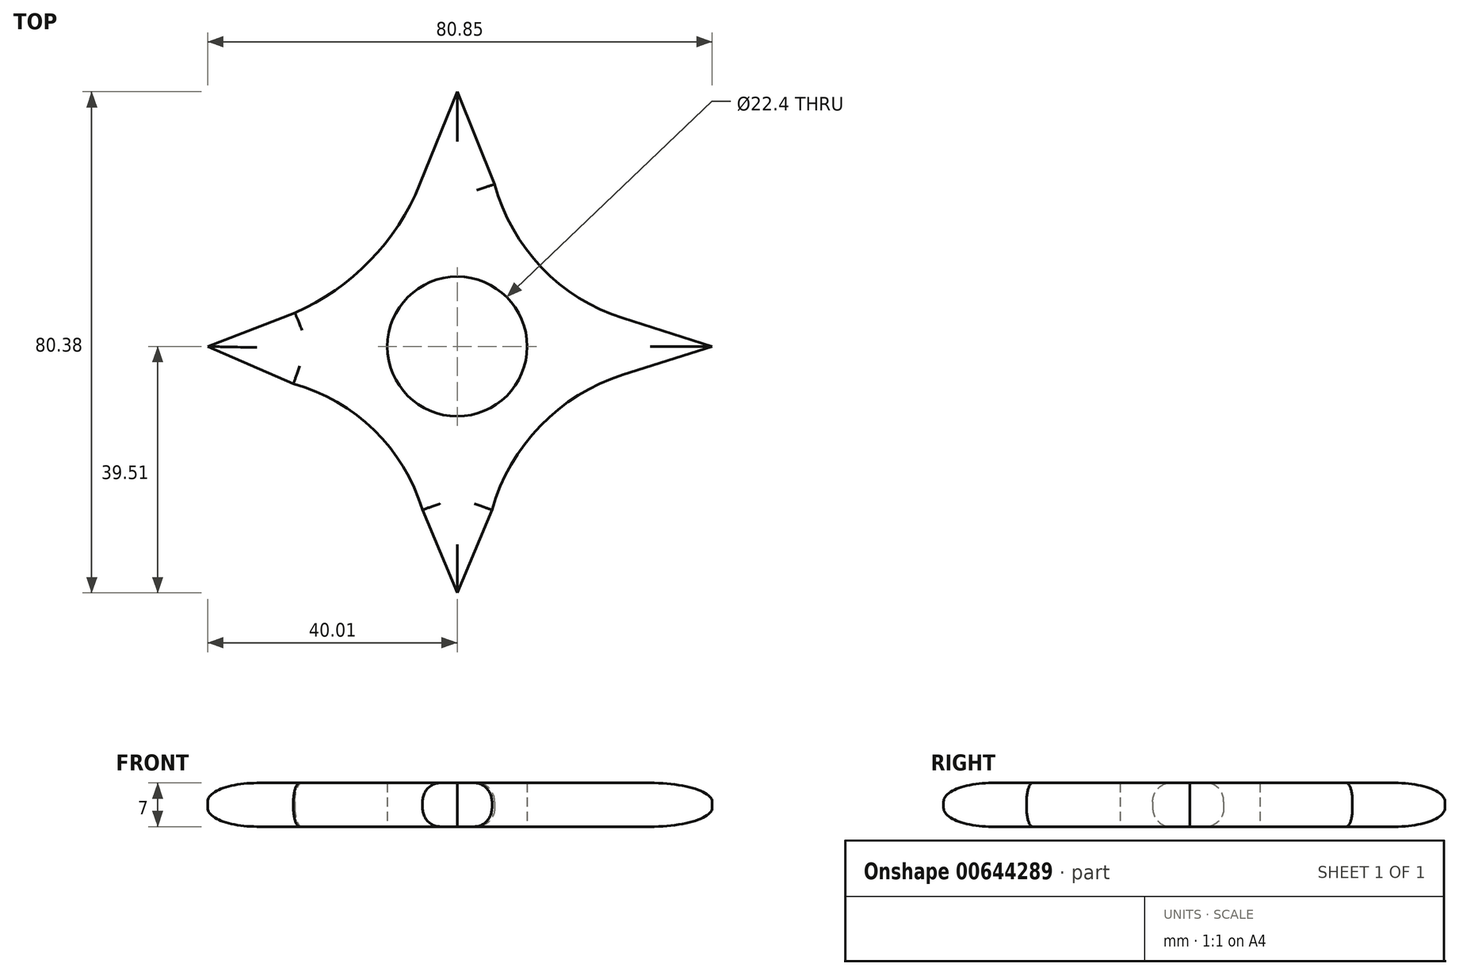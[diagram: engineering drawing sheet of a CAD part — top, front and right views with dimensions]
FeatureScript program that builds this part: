
annotation { "Feature Type Name" : "Feature", "Feature Type Description" : "" }
export const myFeature = defineFeature(function(context is Context, id is Id, definition is map)
    precondition{}
    {
        {
            var Q0;
            Q0=qCreatedBy(makeId("Top.planeOp"),FACE);
            var sketch = newSketch(context, id + "F0", { "sketchPlane" : qUnion([Q0])});
            skCircle(sketch, "E0", {"center": v(0, 0) * mm, "radius": 11.2 * mm});
            skLineSegment(sketch, "E1", {"start": v(0, 11.2) * mm, "end": v(0, 26.2) * mm});
            skLineSegment(sketch, "E2", {"start": v(11.2, 0) * mm, "end": v(26.2, 0) * mm});
            skLineSegment(sketch, "E3", {"start": v(0, -11.2) * mm, "end": v(0, -26.2) * mm});
            skLineSegment(sketch, "E4", {"start": v(-11.18, -0.6) * mm, "end": v(-26.17, 0) * mm});
            skLineSegment(sketch, "E5", {"start": v(0, -11.2) * mm, "end": v(5.57, -26.2) * mm});
            skLineSegment(sketch, "E6", {"start": v(0, -11.2) * mm, "end": v(-5.57, -26.2) * mm});
            skLineSegment(sketch, "E7", {"start": v(11.2, 0) * mm, "end": v(26.54, -4.54) * mm});
            skLineSegment(sketch, "E8", {"start": v(11.2, 0) * mm, "end": v(26.54, 4.54) * mm});
            skLineSegment(sketch, "E9", {"start": v(0, 11.2) * mm, "end": v(6, 26.03) * mm});
            skLineSegment(sketch, "E10", {"start": v(0, 11.2) * mm, "end": v(-6, 26.03) * mm});
            skLineSegment(sketch, "E11", {"start": v(-11.18, -0.6) * mm, "end": v(-26.02, 5.4) * mm});
            skLineSegment(sketch, "E12", {"start": v(-11.18, -0.6) * mm, "end": v(-26.25, -5.97) * mm});
            skLineSegment(sketch, "E13", {"start": v(-26.02, 5.4) * mm, "end": v(-40.01, 0) * mm});
            skLineSegment(sketch, "E14", {"start": v(-40.01, 0) * mm, "end": v(-26.25, -5.97) * mm});
            skLineSegment(sketch, "E15", {"start": v(-6, 26.03) * mm, "end": v(0, 40.87) * mm});
            skLineSegment(sketch, "E16", {"start": v(6, 26.03) * mm, "end": v(0, 40.87) * mm});
            skLineSegment(sketch, "E17", {"start": v(26.54, -4.54) * mm, "end": v(40.84, 0) * mm});
            skLineSegment(sketch, "E18", {"start": v(26.54, 4.54) * mm, "end": v(40.84, 0) * mm});
            skLineSegment(sketch, "E19", {"start": v(-5.57, -26.2) * mm, "end": v(0, -39.51) * mm});
            skLineSegment(sketch, "E20", {"start": v(0, -39.51) * mm, "end": v(5.57, -26.2) * mm});
            skPoint(sketch, "E21.visualSharp", {"position": v(6, 26.03) * mm});
            skLineSegment(sketch, "E21.filletArc", {"start": v(6, 26.03) * mm, "end": v(6, 26.03) * mm});
            skArc(sketch, "E22", {"start": v(6, 26.03) * mm, "mid": v(13.52, 12.66) * mm, "end": v(26.54, 4.54) * mm});
            skArc(sketch, "E23", {"start": v(-26.02, 5.4) * mm, "mid": v(-13.99, 13.76) * mm, "end": v(-6, 26.03) * mm});
            skArc(sketch, "E24", {"start": v(26.54, -4.54) * mm, "mid": v(13.32, -12.72) * mm, "end": v(5.57, -26.2) * mm});
            skArc(sketch, "E25", {"start": v(-5.57, -26.2) * mm, "mid": v(-13.31, -13.43) * mm, "end": v(-26.25, -5.97) * mm});
            skSolve(sketch);
        }
        {
            var Q0;
            Q0 = qSketchRegion(id + "F0", true);
            extrude(context, id + "F1", {"entities" : qUnion([Q0]), "depth" : 7 * mm, "offsetDistance" : 25 * mm});
        }
        {
            var Q0;
            Q0=makeQuery(id+"F1.opExtrude","CAP_EDGE",EDGE,{"disambiguationData":[OSD([sQuery(id+"F0.wireOp",EDGE,"E23")])],"isStart":true});
            var Q1;
            Q1=makeQuery(id+"F1.opExtrude","CAP_EDGE",EDGE,{"disambiguationData":[OSD([sQuery(id+"F0.wireOp",EDGE,"E13")])],"isStart":true});
            var Q2;
            Q2=makeQuery(id+"F1.opExtrude","CAP_EDGE",EDGE,{"disambiguationData":[OSD([sQuery(id+"F0.wireOp",EDGE,"E14")])],"isStart":true});
            var Q3;
            Q3=makeQuery(id+"F1.opExtrude","CAP_EDGE",EDGE,{"disambiguationData":[OSD([sQuery(id+"F0.wireOp",EDGE,"E25")])],"isStart":true});
            var Q4;
            Q4=makeQuery(id+"F1.opExtrude","CAP_EDGE",EDGE,{"disambiguationData":[OSD([sQuery(id+"F0.wireOp",EDGE,"E20")])],"isStart":true});
            var Q5;
            Q5=makeQuery(id+"F1.opExtrude","CAP_EDGE",EDGE,{"disambiguationData":[OSD([sQuery(id+"F0.wireOp",EDGE,"E19")])],"isStart":true});
            var Q6;
            Q6=makeQuery(id+"F1.opExtrude","CAP_EDGE",EDGE,{"disambiguationData":[OSD([sQuery(id+"F0.wireOp",EDGE,"E24")])],"isStart":true});
            var Q7;
            Q7=makeQuery(id+"F1.opExtrude","CAP_EDGE",EDGE,{"disambiguationData":[OSD([sQuery(id+"F0.wireOp",EDGE,"E22")])],"isStart":true});
            var Q8;
            Q8=makeQuery(id+"F1.opExtrude","CAP_EDGE",EDGE,{"disambiguationData":[OSD([sQuery(id+"F0.wireOp",EDGE,"E16")])],"isStart":true});
            var Q9;
            Q9=makeQuery(id+"F1.opExtrude","CAP_EDGE",EDGE,{"disambiguationData":[OSD([sQuery(id+"F0.wireOp",EDGE,"E15")])],"isStart":true});
            var Q10;
            Q10=makeQuery(id+"F1.opExtrude","CAP_EDGE",EDGE,{"disambiguationData":[OSD([sQuery(id+"F0.wireOp",EDGE,"E18")])],"isStart":true});
            var Q11;
            Q11=makeQuery(id+"F1.opExtrude","CAP_EDGE",EDGE,{"disambiguationData":[OSD([sQuery(id+"F0.wireOp",EDGE,"E17")])],"isStart":true});
            fillet(context, id + "F2", {"entities" : qUnion([Q0, Q1, Q2, Q3, Q4, Q5, Q6, Q7, Q8, Q9, Q10, Q11]), "radius" : 3 * mm, "tangentPropagation" : true, "allowEdgeOverflow" : false});
        }
        {
            var Q0;
            Q0=makeQuery(id+"F1.opExtrude","CAP_EDGE",EDGE,{"disambiguationData":[OSD([sQuery(id+"F0.wireOp",EDGE,"E22")])],"isStart":false});
            var Q1;
            Q1=makeQuery(id+"F1.opExtrude","CAP_EDGE",EDGE,{"disambiguationData":[OSD([sQuery(id+"F0.wireOp",EDGE,"E23")])],"isStart":false});
            var Q2;
            Q2=makeQuery(id+"F1.opExtrude","CAP_EDGE",EDGE,{"disambiguationData":[OSD([sQuery(id+"F0.wireOp",EDGE,"E25")])],"isStart":false});
            var Q3;
            Q3=makeQuery(id+"F1.opExtrude","CAP_EDGE",EDGE,{"disambiguationData":[OSD([sQuery(id+"F0.wireOp",EDGE,"E24")])],"isStart":false});
            var Q4;
            Q4=makeQuery(id+"F1.opExtrude","CAP_EDGE",EDGE,{"disambiguationData":[OSD([sQuery(id+"F0.wireOp",EDGE,"E20")])],"isStart":false});
            var Q5;
            Q5=makeQuery(id+"F1.opExtrude","CAP_EDGE",EDGE,{"disambiguationData":[OSD([sQuery(id+"F0.wireOp",EDGE,"E19")])],"isStart":false});
            var Q6;
            Q6=makeQuery(id+"F1.opExtrude","CAP_EDGE",EDGE,{"disambiguationData":[OSD([sQuery(id+"F0.wireOp",EDGE,"E17")])],"isStart":false});
            var Q7;
            Q7=makeQuery(id+"F1.opExtrude","CAP_EDGE",EDGE,{"disambiguationData":[OSD([sQuery(id+"F0.wireOp",EDGE,"E18")])],"isStart":false});
            var Q8;
            Q8=makeQuery(id+"F1.opExtrude","CAP_EDGE",EDGE,{"disambiguationData":[OSD([sQuery(id+"F0.wireOp",EDGE,"E15")])],"isStart":false});
            var Q9;
            Q9=makeQuery(id+"F1.opExtrude","CAP_EDGE",EDGE,{"disambiguationData":[OSD([sQuery(id+"F0.wireOp",EDGE,"E16")])],"isStart":false});
            var Q10;
            Q10=makeQuery(id+"F1.opExtrude","CAP_EDGE",EDGE,{"disambiguationData":[OSD([sQuery(id+"F0.wireOp",EDGE,"E13")])],"isStart":false});
            var Q11;
            Q11=makeQuery(id+"F1.opExtrude","CAP_EDGE",EDGE,{"disambiguationData":[OSD([sQuery(id+"F0.wireOp",EDGE,"E14")])],"isStart":false});
            fillet(context, id + "F3", {"entities" : qUnion([Q0, Q1, Q2, Q3, Q4, Q5, Q6, Q7, Q8, Q9, Q10, Q11]), "radius" : 3 * mm, "tangentPropagation" : true, "allowEdgeOverflow" : false});
        }
    });
